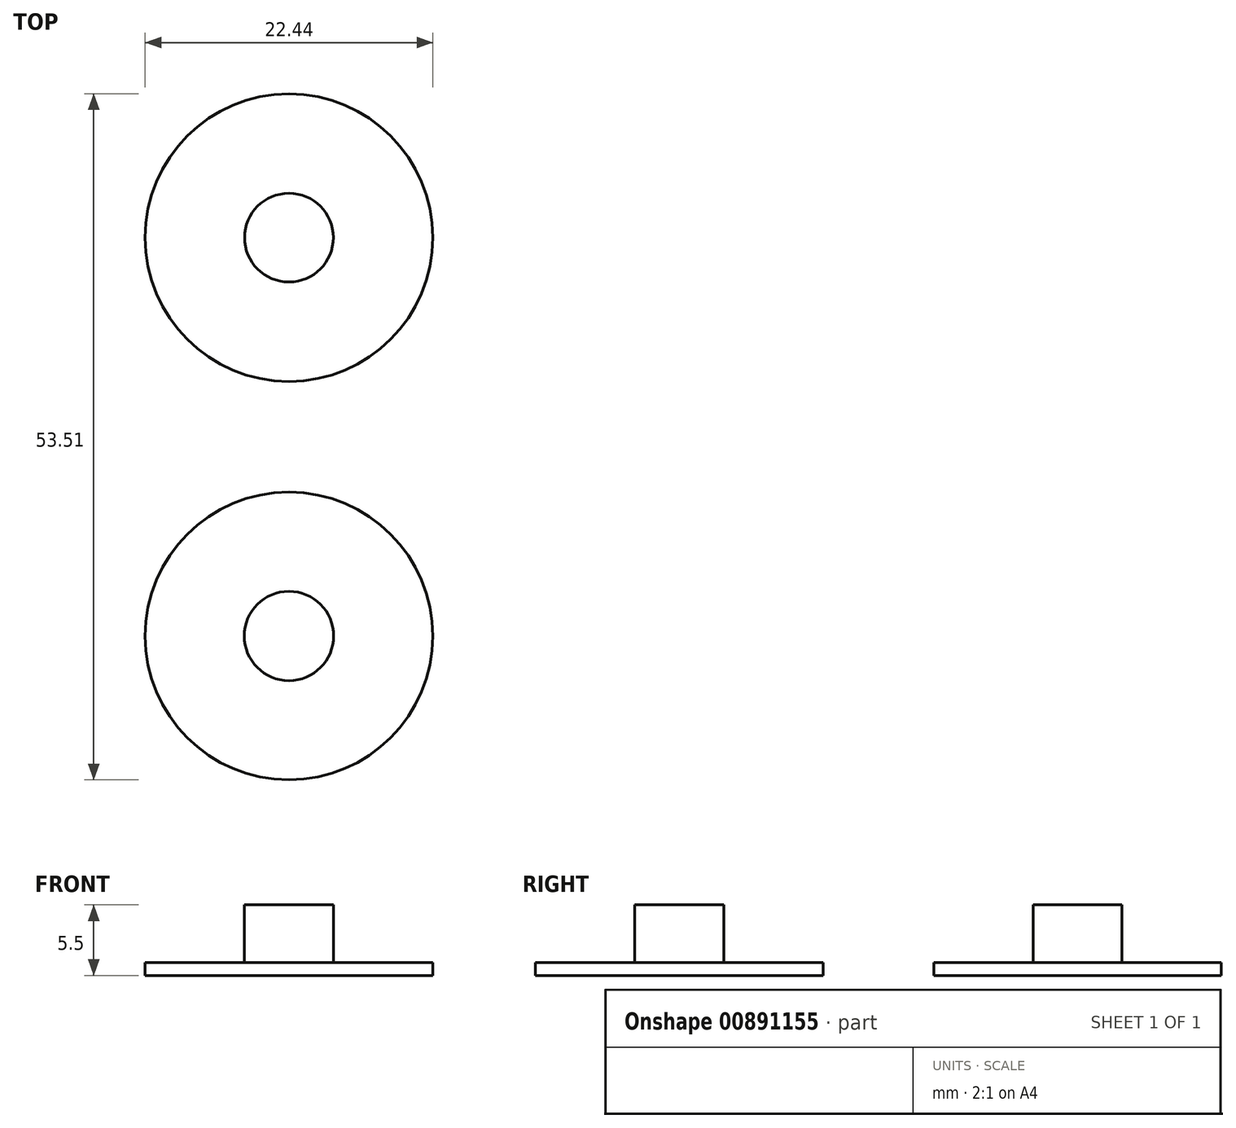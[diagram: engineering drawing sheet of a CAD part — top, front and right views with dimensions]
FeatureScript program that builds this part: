
annotation { "Feature Type Name" : "Feature", "Feature Type Description" : "" }
export const myFeature = defineFeature(function(context is Context, id is Id, definition is map)
    precondition{}
    {
        {
            var Q0;
            Q0=qCreatedBy(makeId("Top.planeOp"),FACE);
            var sketch = newSketch(context, id + "F0", { "sketchPlane" : qUnion([Q0])});
            skCircle(sketch, "E0", {"center": v(0, 0) * mm, "radius": 11.22 * mm});
            skCircle(sketch, "E1", {"center": v(0, -31.07) * mm, "radius": 11.22 * mm});
            skSolve(sketch);
        }
        {
            var Q0;
            Q0 = qSketchRegion(id + "F0", true);
            extrude(context, id + "F1", {"entities" : qUnion([Q0]), "depth" : 1 * mm, "offsetDistance" : 25 * mm});
        }
        {
            var Q0;
            Q0=makeQuery(id+"F1.opExtrude","CAP_FACE",FACE,{"disambiguationData":[OSD([sQuery(id+"F0.wireOp",EDGE,"E0")])],"isStart":false});
            var sketch = newSketch(context, id + "F2", { "sketchPlane" : qUnion([Q0])});
            skCircle(sketch, "E2", {"center": v(0, 0) * mm, "radius": 3.46 * mm});
            skCircle(sketch, "E3", {"center": v(0, -31.07) * mm, "radius": 3.49 * mm});
            skSolve(sketch);
        }
        {
            var Q0;
            Q0=makeQuery(id+"F2.imprint","IMPRINT",FACE,{"disambiguationData":[TD([[makeQuery(id+"F2.imprint","IMPRINT",EDGE,{"derivedFrom":sQuery(id+"F2.wireOp",EDGE,"E2")}),1.0]])]});
            var Q1;
            Q1=makeQuery(id+"F2.imprint","IMPRINT",FACE,{"disambiguationData":[TD([[makeQuery(id+"F2.imprint","IMPRINT",EDGE,{"derivedFrom":sQuery(id+"F2.wireOp",EDGE,"E3")}),1.0]])]});
            extrude(context, id + "F3", {"entities" : qUnion([Q0, Q1]), "depth" : 4.5 * mm, "offsetDistance" : 25 * mm});
        }
    });
